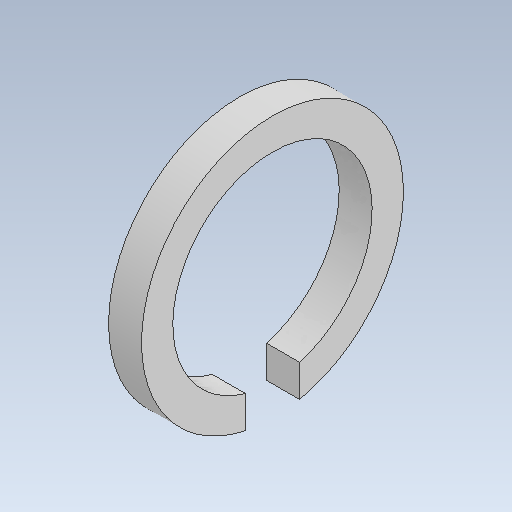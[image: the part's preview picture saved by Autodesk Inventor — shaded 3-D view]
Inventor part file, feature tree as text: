
AUTODESK INVENTOR PART (.ipt)
format: ipt  version: 2021 (Build 250183000, 183)  size: 116,224 bytes
history: native  units: mm
features: extrude x2, sketch x2
ambient origin geometry x8: Origin, YZ Plane, XZ Plane, XY Plane, X Axis, Y Axis, Z Axis, Center Point
bodies: Solid1 (feature_tree)
feature tree (4):
  extrude  "Extrusion1"  Depth=9.5mm
  extrude  "Extrusion2"  Depth=10.0mm
  sketch  "Sketch1"  dims[d0=60.5mm d1=9.5mm]
  sketch  "Sketch2"  dims[d2=10.0mm d3=0.0mm d4=8.218012mm d5=8.218012mm d6=10.0mm d7=0.0mm]
